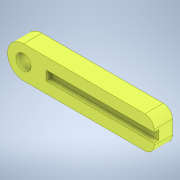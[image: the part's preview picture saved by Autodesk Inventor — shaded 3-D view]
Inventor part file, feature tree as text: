
AUTODESK INVENTOR PART (.ipt)
format: ipt  version: 2020 (Build 240168000, 168)  size: 127,488 bytes
history: native  units: mm
features: extrude x2, sketch x2
ambient origin geometry x8: Origin, YZ Plane, XZ Plane, XY Plane, X Axis, Y Axis, Z Axis, Center Point
bodies: Solid1 (feature_tree)
feature tree (4):
  extrude  "Extrusion1"  Depth=7.0mm
  extrude  "Extrusion2"  Depth=1.0mm
  sketch  "Sketch1"  dims[d0=3.3mm d1=7.0mm]
  sketch  "Sketch2"  dims[d2=2.0mm d3=28.5mm d4=4.0mm d5=0.0mm d6=2.0mm d7=5.0mm d8=1.0mm d9=0.0mm]
